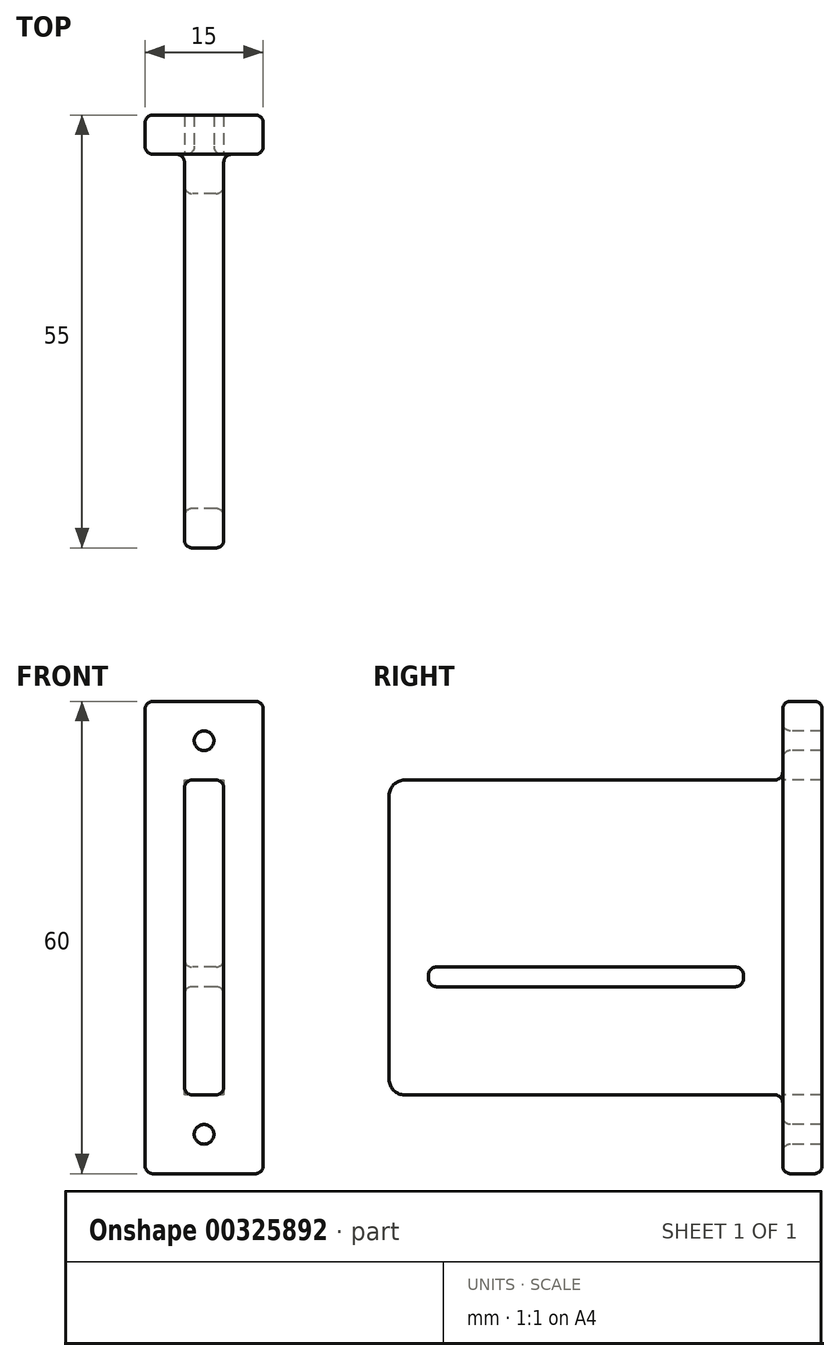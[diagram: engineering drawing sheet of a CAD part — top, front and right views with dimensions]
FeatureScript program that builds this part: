
annotation { "Feature Type Name" : "Feature", "Feature Type Description" : "" }
export const myFeature = defineFeature(function(context is Context, id is Id, definition is map)
    precondition{}
    {
        {
            var Q0;
            Q0=qCreatedBy(makeId("Right.planeOp"),FACE);
            var sketch = newSketch(context, id + "F0", { "sketchPlane" : qUnion([Q0])});
            skLineSegment(sketch, "E0.bottom", {"start": v(-25, -20) * mm, "end": v(25, -20) * mm});
            skLineSegment(sketch, "E0.top", {"start": v(-25, 20) * mm, "end": v(25, 20) * mm});
            skLineSegment(sketch, "E0.left", {"start": v(-25, -20) * mm, "end": v(-25, 20) * mm});
            skLineSegment(sketch, "E0.right", {"start": v(25, -20) * mm, "end": v(25, 20) * mm});
            skPoint(sketch, "E0.middle", {"position": v(0, 0) * mm});
            skLineSegment(sketch, "E1.bottom", {"start": v(-20, -6.25) * mm, "end": v(20, -6.25) * mm});
            skLineSegment(sketch, "E1.top", {"start": v(-20, -3.75) * mm, "end": v(20, -3.75) * mm});
            skLineSegment(sketch, "E1.left", {"start": v(-20, -6.25) * mm, "end": v(-20, -3.75) * mm});
            skLineSegment(sketch, "E1.right", {"start": v(20, -6.25) * mm, "end": v(20, -3.75) * mm});
            skPoint(sketch, "E1.middle", {"position": v(0, -5) * mm});
            skSolve(sketch);
        }
        {
            var Q0;
            Q0=makeQuery(id+"F0.imprint","IMPRINT",FACE,{"disambiguationData":[TD([[makeQuery(id+"F0.imprint","IMPRINT",EDGE,{"derivedFrom":sQuery(id+"F0.wireOp",EDGE,"E0.bottom")}),1.0]])]});
            extrude(context, id + "F1", {"entities" : qUnion([Q0]), "endBound" : BoundingType.SYMMETRIC, "depth" : 5 * mm});
        }
        {
            var Q0;
            Q0=makeQuery(id+"F1.opExtrude","SWEPT_EDGE",EDGE,{"disambiguationData":[OSD([sQuery(id+"F0.wireOp",EDGE,"E1.bottom"),sQuery(id+"F0.wireOp",EDGE,"E1.left")])]});
            var Q1;
            Q1=makeQuery(id+"F1.opExtrude","SWEPT_EDGE",EDGE,{"disambiguationData":[OSD([sQuery(id+"F0.wireOp",EDGE,"E1.bottom"),sQuery(id+"F0.wireOp",EDGE,"E1.right")])]});
            var Q2;
            Q2=makeQuery(id+"F1.opExtrude","SWEPT_EDGE",EDGE,{"disambiguationData":[OSD([sQuery(id+"F0.wireOp",EDGE,"E1.top"),sQuery(id+"F0.wireOp",EDGE,"E1.right")])]});
            var Q3;
            Q3=makeQuery(id+"F1.opExtrude","SWEPT_EDGE",EDGE,{"disambiguationData":[OSD([sQuery(id+"F0.wireOp",EDGE,"E1.top"),sQuery(id+"F0.wireOp",EDGE,"E1.left")])]});
            fillet(context, id + "F2", {"entities" : qUnion([Q0, Q1, Q2, Q3]), "radius" : 1 * mm, "tangentPropagation" : true, "allowEdgeOverflow" : false});
        }
        {
            var Q0;
            Q0=makeQuery(id+"F1.opExtrude","SWEPT_EDGE",EDGE,{"disambiguationData":[OSD([sQuery(id+"F0.wireOp",EDGE,"E0.top"),sQuery(id+"F0.wireOp",EDGE,"E0.left")])]});
            var Q1;
            Q1=makeQuery(id+"F1.opExtrude","SWEPT_EDGE",EDGE,{"disambiguationData":[OSD([sQuery(id+"F0.wireOp",EDGE,"E0.bottom"),sQuery(id+"F0.wireOp",EDGE,"E0.left")])]});
            fillet(context, id + "F3", {"entities" : qUnion([Q0, Q1]), "radius" : 2 * mm, "allowEdgeOverflow" : false});
        }
        {
            var Q0;
            Q0=makeQuery(id+"F1.opExtrude","SWEPT_FACE",FACE,{"disambiguationData":[OSD([sQuery(id+"F0.wireOp",EDGE,"E0.right")])]});
            var sketch = newSketch(context, id + "F4", { "sketchPlane" : qUnion([Q0])});
            skLineSegment(sketch, "E2.bottom", {"start": v(-7.5, -30) * mm, "end": v(7.5, -30) * mm});
            skLineSegment(sketch, "E2.top", {"start": v(-7.5, 30) * mm, "end": v(7.5, 30) * mm});
            skLineSegment(sketch, "E2.left", {"start": v(-7.5, -30) * mm, "end": v(-7.5, 30) * mm});
            skLineSegment(sketch, "E2.right", {"start": v(7.5, -30) * mm, "end": v(7.5, 30) * mm});
            skPoint(sketch, "E2.middle", {"position": v(0, 0) * mm});
            skCircle(sketch, "E3", {"center": v(0, 25) * mm, "radius": 1.25 * mm});
            skCircle(sketch, "E4", {"center": v(0, -25) * mm, "radius": 1.25 * mm});
            skSolve(sketch);
        }
        {
            var Q0;
            Q0=makeQuery(id+"F4.imprint","IMPRINT",FACE,{"disambiguationData":[TD([[makeQuery(id+"F4.imprint","IMPRINT",EDGE,{"derivedFrom":sQuery(id+"F4.wireOp",EDGE,"E2.bottom")}),1.0]])]});
            extrude(context, id + "F5", {"entities" : qUnion([Q0]), "operationType" : NewBodyOperationType.ADD, "depth" : 5 * mm});
        }
        {
            var Q0;
            Q0 = qSketchRegion(id + "F4", true);
            extrude(context, id + "F6", {"entities" : qUnion([Q0]), "operationType" : NewBodyOperationType.ADD, "depth" : 0 * mm});
        }
        {
            var Q0;
            Q0=makeQuery(id+"F1.opExtrude","CAP_FACE",FACE,{"disambiguationData":[OSD([sQuery(id+"F0.wireOp",EDGE,"E0.bottom"),sQuery(id+"F0.wireOp",EDGE,"E0.top"),sQuery(id+"F0.wireOp",EDGE,"E0.left"),sQuery(id+"F0.wireOp",EDGE,"E0.right"),sQuery(id+"F0.wireOp",EDGE,"E1.bottom"),sQuery(id+"F0.wireOp",EDGE,"E1.top"),sQuery(id+"F0.wireOp",EDGE,"E1.left"),sQuery(id+"F0.wireOp",EDGE,"E1.right")])],"isStart":false});
            var Q1;
            {var subQ0=sQuery(id+"F4.wireOp",EDGE,"E4");var subQ1=sQuery(id+"F4.wireOp",EDGE,"E3");var subQ2=sQuery(id+"F4.wireOp",EDGE,"E2.right");var subQ3=sQuery(id+"F4.wireOp",EDGE,"E2.left");var subQ4=sQuery(id+"F4.wireOp",EDGE,"E2.top");var subQ5=sQuery(id+"F4.wireOp",EDGE,"E2.bottom");Q1=makeQuery(id+"F6.boolean.opBoolean","MERGE",FACE,{"derivedFrom":[makeQuery(id+"F5.opExtrude","CAP_FACE",FACE,{"disambiguationData":[OSD([sQuery(id+"F0.wireOp",EDGE,"E0.bottom"),sQuery(id+"F0.wireOp",EDGE,"E0.top"),sQuery(id+"F0.wireOp",EDGE,"E0.right"),subQ5,subQ4,subQ3,subQ2,subQ1,subQ0])],"isStart":true}),makeQuery(id+"F6.opExtrude","CAP_FACE",FACE,{"disambiguationData":[OSD([subQ5,subQ4,subQ3,subQ2,subQ1,subQ0])],"isStart":true})]});}
            var Q2;
            Q2=makeQuery(id+"FodPEgBTVZ07hKg_2.boolean.opBoolean","MERGE",FACE,{"derivedFrom":[makeQuery(id+"F5.opExtrude","SWEPT_FACE",FACE,{"disambiguationData":[OSD([sQuery(id+"F4.wireOp",EDGE,"E2.left")])]}),makeQuery(id+"FodPEgBTVZ07hKg_2.opExtrude","SWEPT_FACE",FACE,{"disambiguationData":[OSD([sQuery(id+"Fj3EQ2RL6Ki28n9_2.wireOp",EDGE,"qcGRP9yz-Li6l-JZeM-ANsN-kn79OEhYuhHU")])]})]});
            var Q3;
            Q3=makeQuery(id+"FodPEgBTVZ07hKg_2.boolean.opBoolean","MERGE",FACE,{"derivedFrom":[makeQuery(id+"F5.opExtrude","SWEPT_FACE",FACE,{"disambiguationData":[OSD([sQuery(id+"F4.wireOp",EDGE,"E2.top")])]}),makeQuery(id+"FodPEgBTVZ07hKg_2.opExtrude","CAP_FACE",FACE,{"disambiguationData":[OSD([sQuery(id+"Fj3EQ2RL6Ki28n9_2.wireOp",EDGE,"IENDHWsx-3k5b-HoaW-uCgJ-ysnJl5m1Nj7w"),sQuery(id+"Fj3EQ2RL6Ki28n9_2.wireOp",EDGE,"qcGRP9yz-Li6l-JZeM-ANsN-kn79OEhYuhHU"),sQuery(id+"Fj3EQ2RL6Ki28n9_2.wireOp",EDGE,"DZ3OwOVS-mfPE-upgq-juTd-KWtCHAn6gbPQ")])],"isStart":true})]});
            var Q4;
            Q4=makeQuery(id+"F1.opExtrude","CAP_FACE",FACE,{"disambiguationData":[OSD([sQuery(id+"F0.wireOp",EDGE,"E0.bottom"),sQuery(id+"F0.wireOp",EDGE,"E0.top"),sQuery(id+"F0.wireOp",EDGE,"E0.left"),sQuery(id+"F0.wireOp",EDGE,"E0.right"),sQuery(id+"F0.wireOp",EDGE,"E1.bottom"),sQuery(id+"F0.wireOp",EDGE,"E1.top"),sQuery(id+"F0.wireOp",EDGE,"E1.left"),sQuery(id+"F0.wireOp",EDGE,"E1.right")])],"isStart":true});
            var Q5;
            Q5=makeQuery(id+"F5.opExtrude","SWEPT_FACE",FACE,{"disambiguationData":[OSD([sQuery(id+"F4.wireOp",EDGE,"E2.right")])]});
            var Q6;
            {var subQ0=sQuery(id+"F4.wireOp",EDGE,"E2.bottom");Q6=makeQuery(id+"FodPEgBTVZ07hKg_2.boolean.opBoolean","MERGE",FACE,{"derivedFrom":[makeQuery(id+"F5.opExtrude","SWEPT_FACE",FACE,{"disambiguationData":[OSD([subQ0])]}),makeQuery(id+"FodPEgBTVZ07hKg_2.opExtrude","CAP_FACE",FACE,{"disambiguationData":[OSD([subQ0])],"isStart":false})]});}
            fillet(context, id + "F7", {"entities" : qUnion([Q0, Q1, Q2, Q3, Q4, Q5, Q6]), "radius" : 1 * mm, "tangentPropagation" : true, "allowEdgeOverflow" : false});
        }
    });
